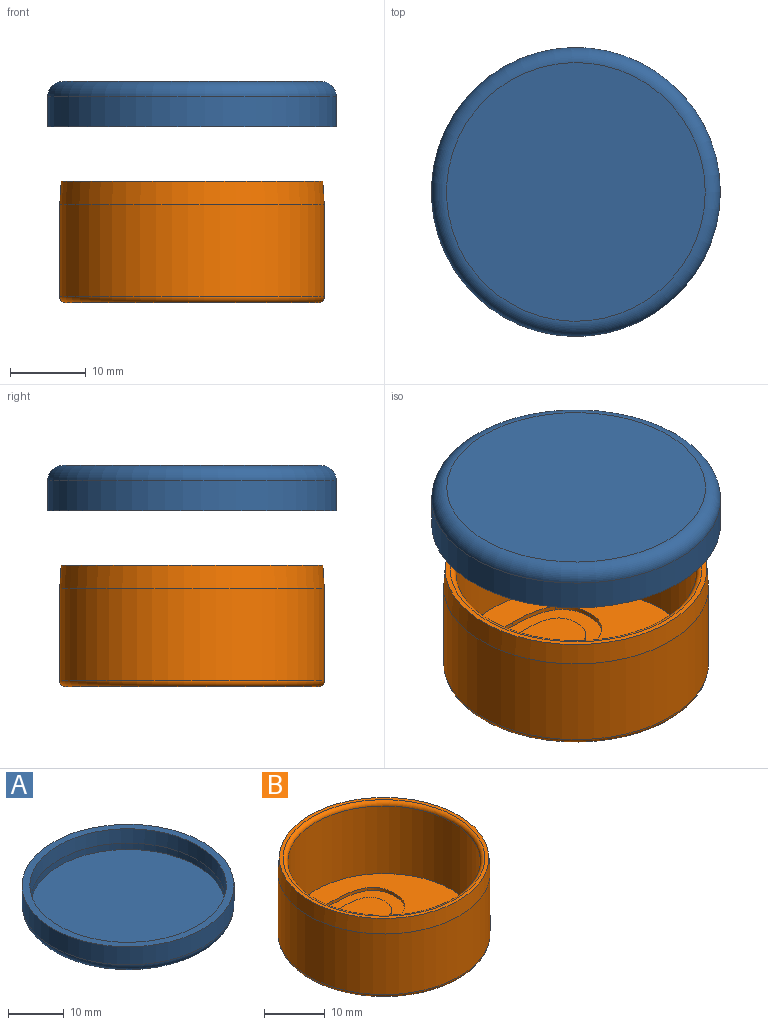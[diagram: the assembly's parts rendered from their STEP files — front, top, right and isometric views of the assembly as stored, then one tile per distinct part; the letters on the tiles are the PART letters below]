
ASSEMBLY  parts=2 mates=1
PART A: 7 faces, bbox 41.3x41.3x6 mm
  f0: plane 35x35mm, normal (0,0,1), area 962.1mm2, adj f1
  f1: cylinder r=17.5mm len=35mm, axis (0,0,-1), area 153.9mm2, adj f0,f5
  f2: cylinder r=19.1mm len=38.2mm, axis (0,0,-1), area 480mm2, adj f3,f6
  f3: plane 38.2x38.2mm, normal (0,0,1), area 161.9mm2, adj f2,f5
  f4: plane 34.2x34.2mm, normal (0,0,-1), area 918.6mm2, adj f6
  f5: cone r=17.5mm half-angle=3.8deg, axis (0,0,1), area 332.5mm2, adj f1,f3
  f6: torus R=17.1mm, axis (0,0,1), area 362.7mm2, adj f2,f4
PART B: 36 faces, bbox 37.9x37.9x16 mm
  f0: plane 23.18x0.6mm, normal (1,0,0), area 13.9mm2, adj f1,f10,f11,f19
  f1: plane 6.55x0.6mm, normal (0,-1,0), area 3.9mm2, adj f0,f2,f11,f19
  f2: extruded ~6.67x1.38mm, area 4.1mm2, adj f1,f3,f11,f19
  f3: extruded ~4.36x2.06mm, area 3mm2, adj f2,f4,f11,f19
  f4: extruded ~3.4x1.15mm, area 2.2mm2, adj f3,f5,f11,f19
  f5: extruded ~3.36x1.74mm, area 2.3mm2, adj f4,f6,f11,f19
  f6: plane 0.6x0.16mm, normal (-1,0,0), area 0.1mm2, adj f5,f7,f11,f19
  f7: extruded ~5.55x5.28mm, area 5.1mm2, adj f6,f8,f11,f19
  f8: extruded ~4.85x2.1mm, area 3.3mm2, adj f7,f9,f11,f19
  f9: extruded ~5.87x1.75mm, area 3.8mm2, adj f8,f10,f11,f19
  f10: plane 8.09x0.6mm, normal (0,1,0), area 4.9mm2, adj f0,f9,f11,f19
  f11: plane 31.8x31.8mm, normal (0,0,1), area 460.3mm2, adj f0,f1,f2,f3,f4,f5,f6,f7
  f12: plane 33.5x33.5mm, normal (0,0,-1), area 881.4mm2, adj f17
  f13: cylinder r=15.9mm len=31.8mm, axis (0,0,-1), area 1363.7mm2, adj f11,f18
  f14: cylinder r=17.5mm len=35mm, axis (0,0,-1), area 1347mm2, adj f16,f17
  f15: plane 34.6x34.6mm, normal (0,0,1), area 69.3mm2, adj f16,f18
  f16: cone r=17.3mm half-angle=3.8deg, axis (0,0,-1), area 328.7mm2, adj f14,f15
  f17: torus R=16.75mm, axis (0,0,1), area 127.5mm2, adj f12,f14
  f18: torus R=16.65mm, axis (0,0,1), area 119.7mm2, adj f13,f15
  f19: plane 23.18x16.06mm, normal (0,0,1), area 183.2mm2, adj f0,f1,f2,f3,f4,f5,f6,f7
  f20: plane 9.8x7.59mm, normal (0,0,1), area 68mm2, adj f21,f22,f23,f24,f25,f26,f27
  f21: extruded ~4.11x0.9mm, area 2.6mm2, adj f19,f20,f22,f27
  f22: extruded ~3.02x1.25mm, area 2mm2, adj f19,f20,f21,f23
  f23: extruded ~2.82x1.4mm, area 2mm2, adj f19,f20,f22,f24
  f24: extruded ~4.44x0.86mm, area 2.7mm2, adj f19,f20,f23,f25
  f25: plane 3.97x0.6mm, normal (0,1,0), area 2.4mm2, adj f19,f20,f24,f26
  f26: plane 7.59x0.6mm, normal (-1,0,0), area 4.6mm2, adj f19,f20,f25,f27
  f27: plane 4.44x0.6mm, normal (0,-1,0), area 2.7mm2, adj f19,f20,f21,f26
  f28: plane 10.48x8.67mm, normal (0,0,1), area 82.8mm2, adj f29,f30,f31,f32,f33,f34,f35
  f29: plane 4.84x0.6mm, normal (0,-1,0), area 2.9mm2, adj f19,f28,f30,f35
  f30: extruded ~4.22x1.09mm, area 2.7mm2, adj f19,f28,f29,f31
  f31: extruded ~3.4x1.42mm, area 2.3mm2, adj f19,f28,f30,f32
  f32: extruded ~3.17x1.45mm, area 2.2mm2, adj f19,f28,f31,f33
  f33: extruded ~4.41x1.01mm, area 2.8mm2, adj f19,f28,f32,f34
  f34: plane 4.62x0.6mm, normal (0,1,0), area 2.8mm2, adj f19,f28,f33,f35
  f35: plane 8.67x0.6mm, normal (-1,0,0), area 5.2mm2, adj f19,f28,f29,f34
PLACE A rot(axis=(1,0,0),180deg) t=(0,0,29.22)mm
PLACE B at identity fixed
MATE slider B.f13 <-> A.f2  axis (0,0,-1) through (0,0,8.43)mm
